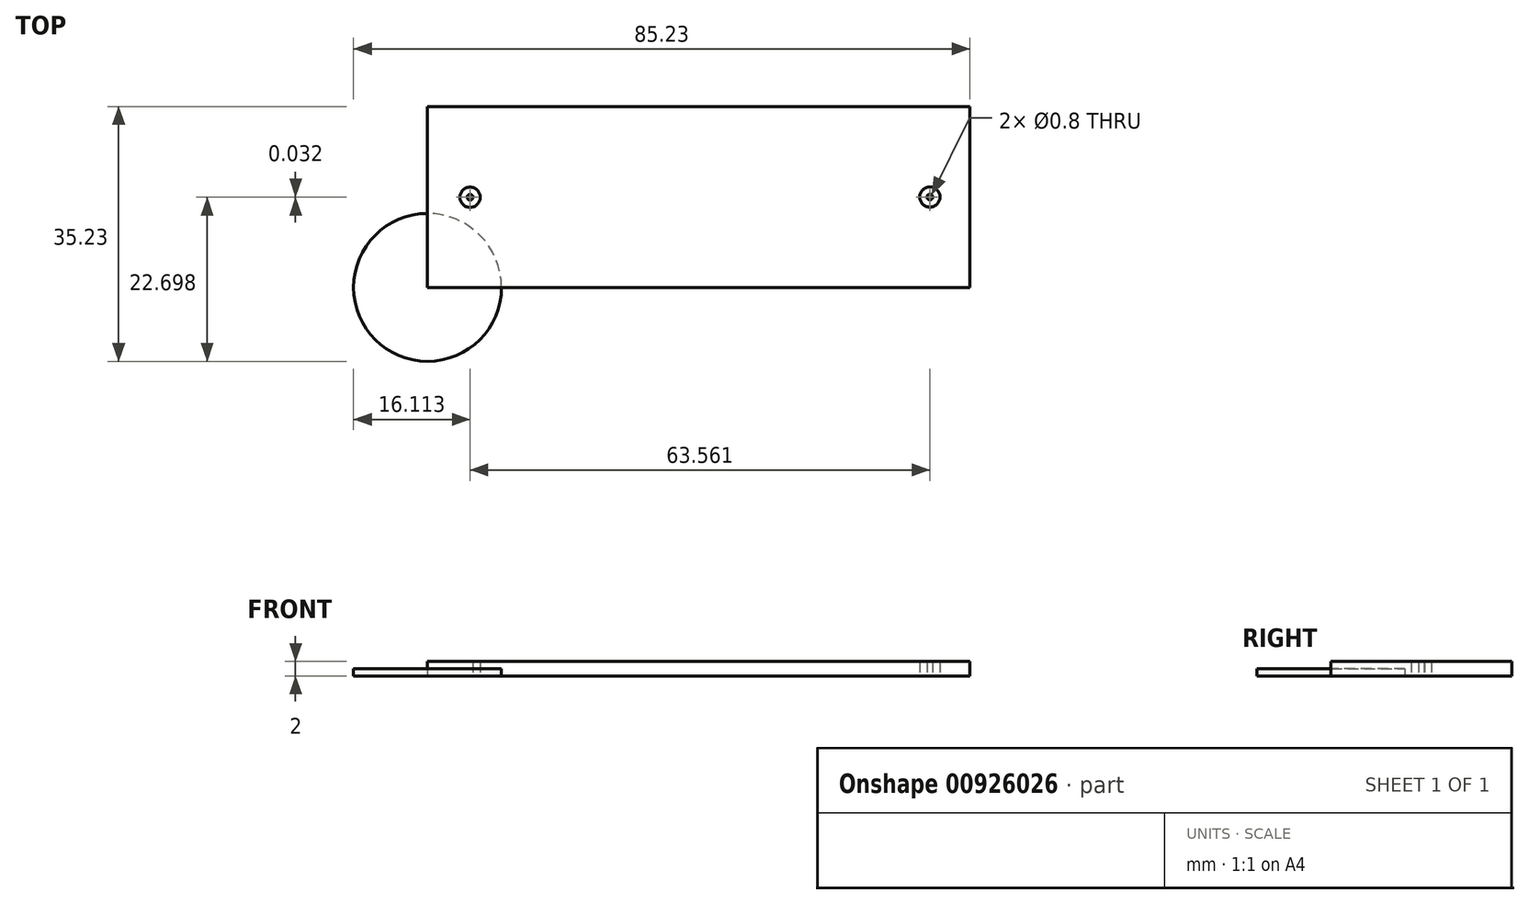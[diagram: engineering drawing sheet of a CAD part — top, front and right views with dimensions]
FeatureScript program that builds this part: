
annotation { "Feature Type Name" : "Feature", "Feature Type Description" : "" }
export const myFeature = defineFeature(function(context is Context, id is Id, definition is map)
    precondition{}
    {
        {
            var Q0;
            Q0=qCreatedBy(makeId("Top.planeOp"),FACE);
            var sketch = newSketch(context, id + "F0", { "sketchPlane" : qUnion([Q0])});
            skLineSegment(sketch, "E0.bottom", {"start": v(0, 0) * mm, "end": v(75, 0) * mm});
            skLineSegment(sketch, "E0.top", {"start": v(0, 25) * mm, "end": v(75, 25) * mm});
            skLineSegment(sketch, "E0.left", {"start": v(0, 0) * mm, "end": v(0, 25) * mm});
            skLineSegment(sketch, "E0.right", {"start": v(75, 0) * mm, "end": v(75, 25) * mm});
            skSolve(sketch);
        }
        {
            var Q0;
            Q0=qCreatedBy(makeId("Top.planeOp"),FACE);
            var sketch = newSketch(context, id + "F1", { "sketchPlane" : qUnion([Q0])});
            skCircle(sketch, "E1", {"center": v(5.88, 12.47) * mm, "radius": 0.4 * mm});
            skCircle(sketch, "E2", {"center": v(69.44, 12.5) * mm, "radius": 0.4 * mm});
            skCircle(sketch, "E3", {"center": v(5.88, 12.47) * mm, "radius": 1.4 * mm});
            skCircle(sketch, "E4", {"center": v(69.44, 12.5) * mm, "radius": 1.4 * mm});
            skSolve(sketch);
        }
        {
            var Q0;
            Q0=qCreatedBy(makeId("Top.planeOp"),FACE);
            var sketch = newSketch(context, id + "F2", { "sketchPlane" : qUnion([Q0])});
            skLineSegment(sketch, "E5.bottom", {"start": v(0, 0) * mm, "end": v(75, 0) * mm});
            skLineSegment(sketch, "E5.top", {"start": v(0, 25) * mm, "end": v(75, 25) * mm});
            skLineSegment(sketch, "E5.left", {"start": v(0, 0) * mm, "end": v(0, 25) * mm});
            skLineSegment(sketch, "E5.right", {"start": v(75, 0) * mm, "end": v(75, 25) * mm});
            skPoint(sketch, "E6.centerSnap0", {"position": v(0, 12.5) * mm});
            skLineSegment(sketch, "E7.left", {"start": v(15.96, 7.36) * mm, "end": v(15.96, 11.6) * mm});
            skLineSegment(sketch, "E7.right", {"start": v(16.96, 8.26) * mm, "end": v(16.96, 11.56) * mm});
            skLineSegment(sketch, "E8.trimOffspring", {"start": v(15.96, 13.4) * mm, "end": v(15.96, 17.64) * mm});
            skLineSegment(sketch, "E9.bottom", {"start": v(17.36, 17.14) * mm, "end": v(19.56, 17.14) * mm});
            skLineSegment(sketch, "E9.top", {"start": v(16.36, 18.14) * mm, "end": v(19.56, 18.14) * mm});
            skLineSegment(sketch, "E9.left", {"start": v(15.96, 17.14) * mm, "end": v(15.96, 17.74) * mm});
            skLineSegment(sketch, "E10.bottom", {"start": v(17.36, 7.86) * mm, "end": v(19.56, 7.86) * mm});
            skLineSegment(sketch, "E10.top", {"start": v(16.36, 6.86) * mm, "end": v(19.56, 6.86) * mm});
            skLineSegment(sketch, "E10.left", {"start": v(15.96, 7.86) * mm, "end": v(15.96, 7.26) * mm});
            skLineSegment(sketch, "E11.left", {"start": v(19.96, 9.93) * mm, "end": v(19.96, 8.26) * mm});
            skLineSegment(sketch, "E11.right", {"start": v(20.96, 9.03) * mm, "end": v(20.96, 8.16) * mm});
            skLineSegment(sketch, "E12.left", {"start": v(19.96, 15.07) * mm, "end": v(19.96, 16.74) * mm});
            skLineSegment(sketch, "E12.right", {"start": v(20.96, 15.97) * mm, "end": v(20.96, 16.84) * mm});
            skLineSegment(sketch, "E13.top", {"start": v(20.36, 20.7) * mm, "end": v(35.62, 20.7) * mm});
            skLineSegment(sketch, "E13.left", {"start": v(19.96, 19.7) * mm, "end": v(19.96, 20.3) * mm});
            skLineSegment(sketch, "E14.bottom", {"start": v(21.36, 15.57) * mm, "end": v(24.78, 15.57) * mm});
            skLineSegment(sketch, "E14.top", {"start": v(20.36, 14.57) * mm, "end": v(24.78, 14.57) * mm});
            skLineSegment(sketch, "E14.left", {"start": v(19.96, 15.57) * mm, "end": v(19.96, 14.97) * mm});
            skLineSegment(sketch, "E15.bottom", {"start": v(21.36, 9.43) * mm, "end": v(24.78, 9.43) * mm});
            skLineSegment(sketch, "E15.top", {"start": v(20.36, 10.43) * mm, "end": v(24.78, 10.43) * mm});
            skLineSegment(sketch, "E15.left", {"start": v(19.96, 9.43) * mm, "end": v(19.96, 10.03) * mm});
            skLineSegment(sketch, "E16.bottom", {"start": v(21.36, 5.3) * mm, "end": v(24.78, 5.3) * mm});
            skLineSegment(sketch, "E16.top", {"start": v(20.36, 4.3) * mm, "end": v(35.62, 4.3) * mm});
            skLineSegment(sketch, "E16.left", {"start": v(19.96, 5.3) * mm, "end": v(19.96, 4.7) * mm});
            skLineSegment(sketch, "E17.trimOffspring", {"start": v(19.96, 18.54) * mm, "end": v(19.96, 20.2) * mm});
            skLineSegment(sketch, "E18.trimOffspring", {"start": v(19.96, 6.46) * mm, "end": v(19.96, 4.8) * mm});
            skPoint(sketch, "E19.visualSharp", {"position": v(15.96, 18.14) * mm});
            skArc(sketch, "E19.filletArc", {"start": v(16.36, 18.14) * mm, "mid": v(16.08, 18.02) * mm, "end": v(15.96, 17.74) * mm});
            skPoint(sketch, "E20.visualSharp", {"position": v(16.96, 17.14) * mm});
            skArc(sketch, "E20.filletArc", {"start": v(17.36, 17.14) * mm, "mid": v(17.08, 17.02) * mm, "end": v(16.96, 16.74) * mm});
            skPoint(sketch, "E21.visualSharp", {"position": v(19.96, 18.14) * mm});
            skArc(sketch, "E21.filletArc", {"start": v(19.56, 18.14) * mm, "mid": v(19.85, 18.25) * mm, "end": v(19.96, 18.54) * mm});
            skPoint(sketch, "E22.visualSharp", {"position": v(19.96, 17.14) * mm});
            skArc(sketch, "E22.filletArc", {"start": v(19.96, 16.74) * mm, "mid": v(19.85, 17.02) * mm, "end": v(19.56, 17.14) * mm});
            skPoint(sketch, "E23.visualSharp", {"position": v(15.96, 13) * mm});
            skArc(sketch, "E23.filletArc", {"start": v(15.56, 13) * mm, "mid": v(15.85, 13.12) * mm, "end": v(15.96, 13.4) * mm});
            skPoint(sketch, "E24.visualSharp", {"position": v(15.96, 12) * mm});
            skArc(sketch, "E24.filletArc", {"start": v(15.96, 11.6) * mm, "mid": v(15.85, 11.88) * mm, "end": v(15.56, 12) * mm});
            skPoint(sketch, "E25.visualSharp", {"position": v(15.96, 6.86) * mm});
            skArc(sketch, "E25.filletArc", {"start": v(15.96, 7.26) * mm, "mid": v(16.08, 6.98) * mm, "end": v(16.36, 6.86) * mm});
            skPoint(sketch, "E26.visualSharp", {"position": v(16.96, 7.86) * mm});
            skArc(sketch, "E26.filletArc", {"start": v(16.96, 8.26) * mm, "mid": v(17.08, 7.98) * mm, "end": v(17.36, 7.86) * mm});
            skPoint(sketch, "E27.visualSharp", {"position": v(19.96, 7.86) * mm});
            skArc(sketch, "E27.filletArc", {"start": v(19.56, 7.86) * mm, "mid": v(19.85, 7.98) * mm, "end": v(19.96, 8.26) * mm});
            skPoint(sketch, "E28.visualSharp", {"position": v(19.96, 6.86) * mm});
            skArc(sketch, "E28.filletArc", {"start": v(19.96, 6.46) * mm, "mid": v(19.85, 6.75) * mm, "end": v(19.56, 6.86) * mm});
            skPoint(sketch, "E29.visualSharp", {"position": v(20.96, 9.43) * mm});
            skArc(sketch, "E29.filletArc", {"start": v(21.36, 9.43) * mm, "mid": v(21.08, 9.3) * mm, "end": v(20.96, 9.03) * mm});
            skPoint(sketch, "E30.visualSharp", {"position": v(19.96, 10.43) * mm});
            skArc(sketch, "E30.filletArc", {"start": v(20.36, 10.43) * mm, "mid": v(20.08, 10.3) * mm, "end": v(19.96, 10.03) * mm});
            skPoint(sketch, "E31.visualSharp", {"position": v(19.96, 14.57) * mm});
            skArc(sketch, "E31.filletArc", {"start": v(19.96, 14.97) * mm, "mid": v(20.08, 14.7) * mm, "end": v(20.36, 14.57) * mm});
            skPoint(sketch, "E32.visualSharp", {"position": v(20.96, 15.57) * mm});
            skArc(sketch, "E32.filletArc", {"start": v(20.96, 15.97) * mm, "mid": v(21.08, 15.7) * mm, "end": v(21.36, 15.57) * mm});
            skPoint(sketch, "E33.visualSharp", {"position": v(20.96, 19.7) * mm});
            skArc(sketch, "E33.filletArc", {"start": v(21.36, 19.7) * mm, "mid": v(21.08, 19.58) * mm, "end": v(20.96, 19.3) * mm});
            skPoint(sketch, "E34.visualSharp", {"position": v(19.96, 20.7) * mm});
            skArc(sketch, "E34.filletArc", {"start": v(20.36, 20.7) * mm, "mid": v(20.08, 20.58) * mm, "end": v(19.96, 20.3) * mm});
            skPoint(sketch, "E35.visualSharp", {"position": v(19.96, 4.3) * mm});
            skArc(sketch, "E35.filletArc", {"start": v(19.96, 4.7) * mm, "mid": v(20.08, 4.42) * mm, "end": v(20.36, 4.3) * mm});
            skPoint(sketch, "E36.visualSharp", {"position": v(20.96, 5.3) * mm});
            skArc(sketch, "E36.filletArc", {"start": v(20.96, 5.7) * mm, "mid": v(21.08, 5.42) * mm, "end": v(21.36, 5.3) * mm});
            skArc(sketch, "E37", {"start": v(16.96, 11.56) * mm, "mid": v(16.54, 12.19) * mm, "end": v(15.85, 12.5) * mm});
            skArc(sketch, "E38.MirrorCS", {"start": v(16.96, 13.94) * mm, "mid": v(16.67, 13.01) * mm, "end": v(15.85, 12.5) * mm});
            skLineSegment(sketch, "E39.trimOffspring", {"start": v(16.96, 13.94) * mm, "end": v(16.96, 16.74) * mm});
            skArc(sketch, "E40", {"start": v(20.96, 6.56) * mm, "mid": v(20.61, 7.06) * mm, "end": v(20.09, 7.36) * mm});
            skArc(sketch, "E41.MirrorCS", {"start": v(20.96, 8.16) * mm, "mid": v(20.61, 7.67) * mm, "end": v(20.09, 7.36) * mm});
            skLineSegment(sketch, "E42.trimOffspring", {"start": v(20.96, 6.56) * mm, "end": v(20.96, 5.7) * mm});
            skLineSegment(sketch, "E43", {"start": v(31.53, 12.5) * mm, "end": v(24.78, 14.57) * mm});
            skLineSegment(sketch, "E44", {"start": v(24.78, 10.43) * mm, "end": v(31.53, 12.5) * mm});
            skPoint(sketch, "E45.startSnap0", {"position": v(24.64, 9.43) * mm});
            skArc(sketch, "E46", {"start": v(20.96, 16.84) * mm, "mid": v(20.62, 17.33) * mm, "end": v(20.1, 17.63) * mm});
            skArc(sketch, "E47.MirrorCS", {"start": v(20.96, 18.42) * mm, "mid": v(20.62, 17.93) * mm, "end": v(20.1, 17.63) * mm});
            skArc(sketch, "E48", {"start": v(5.88, 12.87) * mm, "mid": v(5.48, 12.47) * mm, "end": v(5.88, 12.07) * mm});
            skLineSegment(sketch, "E49", {"start": v(5.88, 12.07) * mm, "end": v(15.56, 12) * mm});
            skPoint(sketch, "E50.orphan", {"position": v(5.88, 13.25) * mm});
            skLineSegment(sketch, "E51", {"start": v(5.88, 12.87) * mm, "end": v(15.56, 13) * mm});
            skLineSegment(sketch, "E52", {"start": v(21.36, 19.7) * mm, "end": v(24.78, 19.7) * mm});
            skLineSegment(sketch, "E53", {"start": v(20.96, 19.3) * mm, "end": v(20.96, 18.42) * mm});
            skLineSegment(sketch, "E54", {"start": v(24.78, 9.43) * mm, "end": v(32.9, 7.36) * mm});
            skLineSegment(sketch, "E55", {"start": v(32.9, 7.36) * mm, "end": v(24.78, 5.3) * mm});
            skLineSegment(sketch, "E56", {"start": v(24.78, 19.7) * mm, "end": v(32.9, 17.63) * mm});
            skLineSegment(sketch, "E57", {"start": v(32.9, 17.63) * mm, "end": v(24.78, 15.57) * mm});
            skPoint(sketch, "E58.trimOffspring.start.orphan", {"position": v(16.26, 12.37) * mm});
            skPoint(sketch, "E59.end.orphan", {"position": v(16.26, 12.65) * mm});
            skSolve(sketch);
        }
        {
            var Q0;
            Q0=qCreatedBy(makeId("Top.planeOp"),FACE);
            var sketch = newSketch(context, id + "F3", { "sketchPlane" : qUnion([Q0])});
            skCircle(sketch, "E60", {"center": v(41.77, 12.5) * mm, "radius": 10.25 * mm});
            skLineSegment(sketch, "E61.bottom", {"start": v(0, 0) * mm, "end": v(75, 0) * mm});
            skLineSegment(sketch, "E61.top", {"start": v(0, 25) * mm, "end": v(75, 25) * mm});
            skLineSegment(sketch, "E61.left", {"start": v(0, 0) * mm, "end": v(0, 25) * mm});
            skLineSegment(sketch, "E61.right", {"start": v(75, 0) * mm, "end": v(75, 25) * mm});
            skSolve(sketch);
        }
        {
            var Q0;
            Q0 = qSketchRegion(id + "F0", true);
            extrude(context, id + "F4", {"entities" : qUnion([Q0]), "depth" : 0.4 * mm, "offsetDistance" : 25 * mm});
        }
        {
            var Q0;
            Q0 = qSketchRegion(id + "F3", true);
            extrude(context, id + "F5", {"entities" : qUnion([Q0]), "operationType" : NewBodyOperationType.ADD, "depth" : 1.6 * mm, "offsetDistance" : 25 * mm});
        }
        {
            var Q0;
            Q0 = qSketchRegion(id + "F2", true);
            var Q1;
            Q1=makeQuery(id+"F2.imprint","IMPRINT",FACE,{"disambiguationData":[TD([[makeQuery(id+"F2.imprint","IMPRINT",EDGE,{"derivedFrom":sQuery(id+"F2.wireOp",EDGE,"E11.right")}),1.0]])]});
            var Q2;
            Q2=makeQuery(id+"F2.imprint","IMPRINT",FACE,{"disambiguationData":[TD([[makeQuery(id+"F2.imprint","IMPRINT",EDGE,{"derivedFrom":sQuery(id+"F2.wireOp",EDGE,"E7.right")}),-1.0]])]});
            var Q3;
            Q3=makeQuery(id+"F2.imprint","IMPRINT",FACE,{"disambiguationData":[TD([[makeQuery(id+"F2.imprint","IMPRINT",EDGE,{"derivedFrom":sQuery(id+"F2.wireOp",EDGE,"E12.right")}),-1.0]])]});
            var Q4;
            Q4 = qConstructionFilter(qBodyType(qCreatedBy(id + "F2" ,EDGE), BodyType.WIRE), ConstructionObject.NO);
            extrude(context, id + "F6", {"entities" : qUnion([Q0, Q1, Q2, Q3]), "operationType" : NewBodyOperationType.ADD, "surfaceOperationType" : NewSurfaceOperationType.ADD, "surfaceEntities" : qUnion([Q4]), "depth" : 2 * mm, "offsetDistance" : 25 * mm});
        }
        {
            var Q0;
            Q0 = qSketchRegion(id + "F1", true);
            extrude(context, id + "F7", {"entities" : qUnion([Q0]), "depth" : 2 * mm, "offsetDistance" : 25 * mm});
        }
        {
            var Q0;
            Q0=qCreatedBy(makeId("Top.planeOp"),FACE);
            var sketch = newSketch(context, id + "F8", { "sketchPlane" : qUnion([Q0])});
            skCircle(sketch, "E62", {"center": v(0, 0) * mm, "radius": 10.23 * mm});
            skSolve(sketch);
        }
        {
            var Q0;
            Q0 = qSketchRegion(id + "F8", true);
            extrude(context, id + "F9", {"entities" : qUnion([Q0]), "depth" : 1 * mm, "offsetDistance" : 25 * mm});
        }
    });
